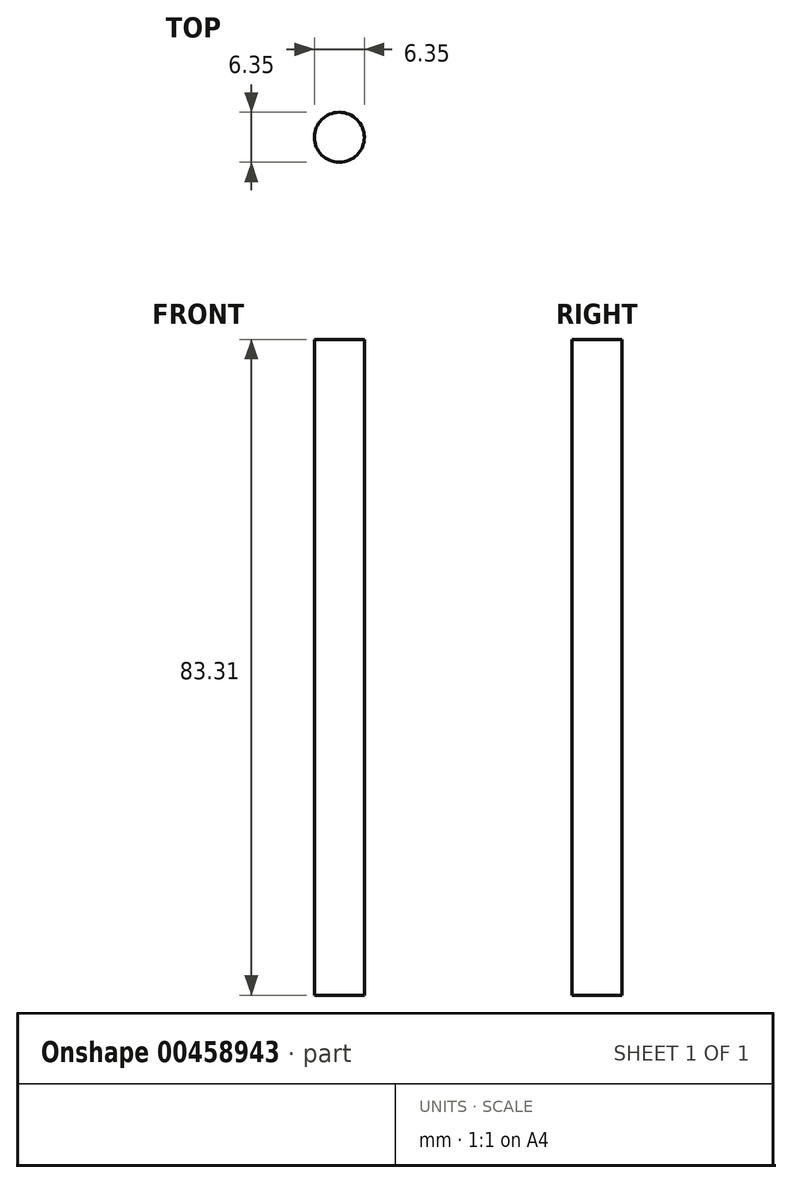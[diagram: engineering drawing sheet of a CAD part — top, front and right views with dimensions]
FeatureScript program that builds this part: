
annotation { "Feature Type Name" : "Feature", "Feature Type Description" : "" }
export const myFeature = defineFeature(function(context is Context, id is Id, definition is map)
    precondition{}
    {
        {
            var Q0;
            Q0=qCreatedBy(makeId("Top.planeOp"),FACE);
            var sketch = newSketch(context, id + "F0", { "sketchPlane" : qUnion([Q0])});
            skCircle(sketch, "E0", {"center": v(-129.33, -22.97) * mm, "radius": 3.18 * mm});
            skSolve(sketch);
        }
        {
            var Q0;
            Q0=makeQuery(id+"F0.imprint","IMPRINT",FACE,{"disambiguationData":[TD([[makeQuery(id+"F0.imprint","IMPRINT",EDGE,{"derivedFrom":sQuery(id+"F0.wireOp",EDGE,"E0")}),1.0]])]});
            extrude(context, id + "F1", {"entities" : qUnion([Q0]), "depth" : 83.31 * mm});
        }
    });
